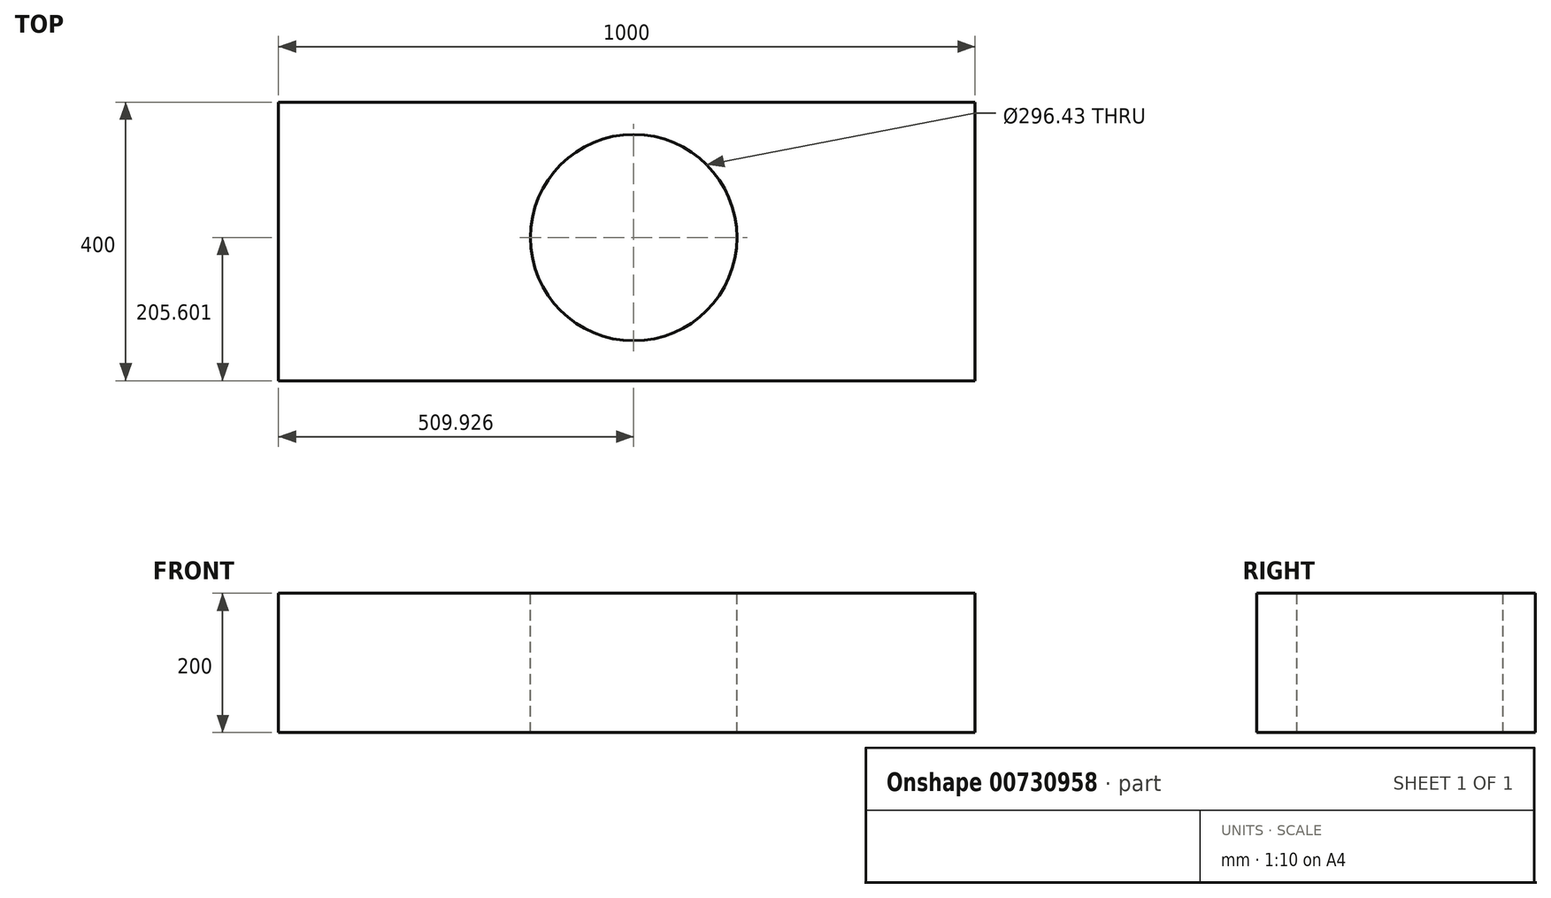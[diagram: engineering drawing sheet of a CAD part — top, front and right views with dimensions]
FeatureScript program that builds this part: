
annotation { "Feature Type Name" : "Feature", "Feature Type Description" : "" }
export const myFeature = defineFeature(function(context is Context, id is Id, definition is map)
    precondition{}
    {
        {
            var Q0;
            Q0=qCreatedBy(makeId("Top.planeOp"),FACE);
            var sketch = newSketch(context, id + "F0", { "sketchPlane" : qUnion([Q0])});
            skLineSegment(sketch, "E0.bottom", {"start": v(-369, 174.55) * mm, "end": v(631, 174.55) * mm});
            skLineSegment(sketch, "E0.top", {"start": v(-369, -225.45) * mm, "end": v(631, -225.45) * mm});
            skLineSegment(sketch, "E0.left", {"start": v(-369, 174.55) * mm, "end": v(-369, -225.45) * mm});
            skLineSegment(sketch, "E0.right", {"start": v(631, 174.55) * mm, "end": v(631, -225.45) * mm});
            skCircle(sketch, "E1", {"center": v(140.93, -19.85) * mm, "radius": 148.21 * mm});
            skSolve(sketch);
        }
        {
            var Q0;
            Q0 = qSketchRegion(id + "F0", true);
            extrude(context, id + "F1", {"entities" : qUnion([Q0]), "oppositeDirection" : true, "depth" : 200 * mm, "offsetDistance" : 25.4 * mm});
        }
    });
